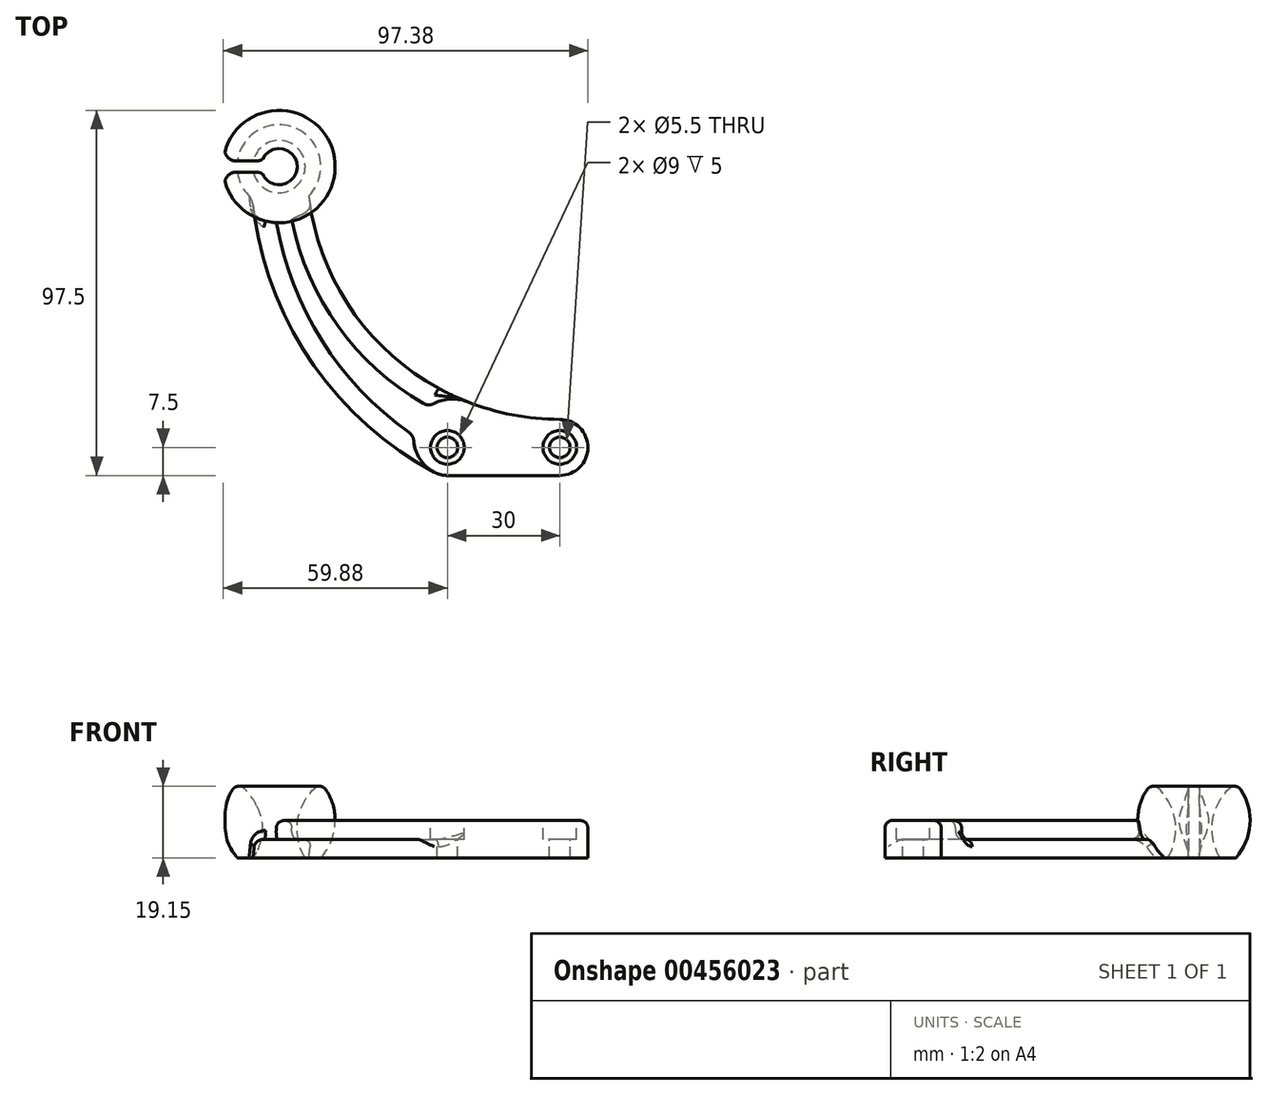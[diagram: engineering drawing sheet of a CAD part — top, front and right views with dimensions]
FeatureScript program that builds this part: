
annotation { "Feature Type Name" : "Feature", "Feature Type Description" : "" }
export const myFeature = defineFeature(function(context is Context, id is Id, definition is map)
    precondition{}
    {
        {
            var Q0;
            Q0=qCreatedBy(makeId("Top.planeOp"),FACE);
            var sketch = newSketch(context, id + "F0", { "sketchPlane" : qUnion([Q0])});
            skLineSegment(sketch, "E0", {"start": v(0, -19.39) * mm, "end": v(0, 110.44) * mm, "construction": true});
            skLineSegment(sketch, "E1.0", {"start": v(10, -19.39) * mm, "end": v(10, 110.44) * mm, "construction": true});
            skLineSegment(sketch, "E2.0", {"start": v(40, -19.39) * mm, "end": v(40, 110.44) * mm, "construction": true});
            skLineSegment(sketch, "E3", {"start": v(61.42, 75) * mm, "end": v(-96.46, 75) * mm, "construction": true});
            skArc(sketch, "E4", {"start": v(-35, 75) * mm, "mid": v(-13.03, 21.97) * mm, "end": v(40, 0) * mm, "construction": true});
            skArc(sketch, "E5.0", {"start": v(-27.5, 75) * mm, "mid": v(-7.73, 27.27) * mm, "end": v(40, 7.5) * mm});
            skArc(sketch, "E6", {"start": v(40, -7.5) * mm, "mid": v(47.5, 0) * mm, "end": v(40, 7.5) * mm});
            skLineSegment(sketch, "E7", {"start": v(40, -7.5) * mm, "end": v(10, -7.5) * mm});
            skArc(sketch, "E8", {"start": v(6.47, -6.62) * mm, "mid": v(8.18, -7.28) * mm, "end": v(10, -7.5) * mm});
            skArc(sketch, "E9", {"start": v(-42.5, 75) * mm, "mid": v(-29.32, 27.4) * mm, "end": v(6.47, -6.62) * mm});
            skPoint(sketch, "E10.orphan", {"position": v(0, -7.5) * mm});
            skLineSegment(sketch, "E11", {"start": v(-42.5, 75) * mm, "end": v(-42.5, 109.62) * mm, "construction": true});
            skLineSegment(sketch, "E12", {"start": v(-42.5, 75) * mm, "end": v(-27.5, 75) * mm});
            skSolve(sketch);
        }
        {
            var Q0;
            Q0 = qSketchRegion(id + "F0", true);
            extrude(context, id + "F1", {"entities" : qUnion([Q0]), "depth" : 5 * mm});
        }
        {
            var Q0;
            Q0=makeQuery(id+"F1.opExtrude","CAP_FACE",FACE,{"disambiguationData":[OSD([sQuery(id+"F0.wireOp",EDGE,"E5.0"),sQuery(id+"F0.wireOp",EDGE,"E6"),sQuery(id+"F0.wireOp",EDGE,"E7"),sQuery(id+"F0.wireOp",EDGE,"E8"),sQuery(id+"F0.wireOp",EDGE,"E9"),sQuery(id+"F0.wireOp",EDGE,"E12")])],"isStart":false});
            var sketch = newSketch(context, id + "F2", { "sketchPlane" : qUnion([Q0])});
            skArc(sketch, "E13.0", {"start": v(6.47, -6.62) * mm, "mid": v(8.18, -7.28) * mm, "end": v(10, -7.5) * mm});
            skLineSegment(sketch, "E14.0", {"start": v(40, -7.5) * mm, "end": v(10, -7.5) * mm});
            skArc(sketch, "E15.0", {"start": v(40, -7.5) * mm, "mid": v(47.5, 0) * mm, "end": v(40, 7.5) * mm});
            skArc(sketch, "E16.0", {"start": v(15.19, 12.23) * mm, "mid": v(27.37, 8.7) * mm, "end": v(40, 7.5) * mm});
            skArc(sketch, "E17", {"start": v(15.19, 12.23) * mm, "mid": v(10.76, 12.94) * mm, "end": v(6.45, 11.72) * mm});
            skArc(sketch, "E18.0", {"start": v(-35, 75) * mm, "mid": v(-13.03, 21.97) * mm, "end": v(40, 0) * mm, "construction": true});
            skArc(sketch, "E19.0", {"start": v(-33, 75) * mm, "mid": v(-23.21, 38.49) * mm, "end": v(3.53, 11.76) * mm});
            skArc(sketch, "E20.0", {"start": v(-37, 75) * mm, "mid": v(-27.27, 35.02) * mm, "end": v(-0.26, 3.99) * mm});
            skArc(sketch, "E21.trimOffspring", {"start": v(1, 1.77) * mm, "mid": v(2.66, -3.13) * mm, "end": v(6.47, -6.62) * mm});
            skPoint(sketch, "E22.orphan", {"position": v(-27.5, 75) * mm});
            skPoint(sketch, "E23.visualSharp", {"position": v(5.12, 10.87) * mm});
            skArc(sketch, "E23.filletArc", {"start": v(3.53, 11.76) * mm, "mid": v(4.98, 11.36) * mm, "end": v(6.45, 11.72) * mm});
            skPoint(sketch, "E24.visualSharp", {"position": v(0.98, 3.12) * mm});
            skArc(sketch, "E24.filletArc", {"start": v(1, 1.77) * mm, "mid": v(0.61, 3.02) * mm, "end": v(-0.26, 3.99) * mm});
            skLineSegment(sketch, "E25", {"start": v(-37, 75) * mm, "end": v(-33, 75) * mm});
            skSolve(sketch);
        }
        {
            var Q0;
            Q0 = qSketchRegion(id + "F2", true);
            extrude(context, id + "F3", {"entities" : qUnion([Q0]), "operationType" : NewBodyOperationType.ADD, "depth" : 5 * mm});
        }
        {
            var Q0;
            Q0=makeQuery(id+"F3.boolean.opBoolean","MERGE",FACE,{"derivedFrom":[makeQuery(id+"F1.opExtrude","SWEPT_FACE",FACE,{"disambiguationData":[OSD([sQuery(id+"F0.wireOp",EDGE,"E12")])]}),makeQuery(id+"F3.opExtrude","SWEPT_FACE",FACE,{"disambiguationData":[OSD([sQuery(id+"F2.wireOp",EDGE,"E25")])]})]});
            var sketch = newSketch(context, id + "F4", { "sketchPlane" : qUnion([Q0])});
            skLineSegment(sketch, "E26", {"start": v(35, -12.3) * mm, "end": v(35, 25.98) * mm, "construction": true});
            skPoint(sketch, "E26.startSnap0", {"position": v(35, 0) * mm});
            skArc(sketch, "E27", {"start": v(22.47, 18.25) * mm, "mid": v(20.04, 8.9) * mm, "end": v(23.82, 0) * mm});
            skLineSegment(sketch, "E28", {"start": v(28, 0) * mm, "end": v(23.82, 0) * mm});
            skArc(sketch, "E29", {"start": v(28, 0) * mm, "mid": v(30.03, 9.73) * mm, "end": v(25.52, 18.6) * mm});
            skPoint(sketch, "E30.visualSharp", {"position": v(23.82, 20) * mm});
            skArc(sketch, "E30.filletArc", {"start": v(25.52, 18.6) * mm, "mid": v(23.92, 19.14) * mm, "end": v(22.47, 18.25) * mm});
            skSolve(sketch);
        }
        {
            var Q0;
            Q0 = qSketchRegion(id + "F4", true);
            var Q1;
            Q1=sQuery(id+"F4.wireOp",EDGE,"E26");
            revolve(context, id + "F5", {"operationType" : NewBodyOperationType.ADD, "entities" : qUnion([Q0]), "axis" : qUnion([Q1]), "revolveType" : RevolveType.FULL});
        }
        {
            var Q0;
            Q0=makeQuery(id+"F3.boolean.opBoolean","MERGE",FACE,{"derivedFrom":[makeQuery(id+"F1.opExtrude","SWEPT_FACE",FACE,{"disambiguationData":[OSD([sQuery(id+"F0.wireOp",EDGE,"E12")])]}),makeQuery(id+"F3.opExtrude","SWEPT_FACE",FACE,{"disambiguationData":[OSD([sQuery(id+"F2.wireOp",EDGE,"E25")])]})]});
            var sketch = newSketch(context, id + "F6", { "sketchPlane" : qUnion([Q0])});
            skArc(sketch, "E31.0", {"start": v(28, 0) * mm, "mid": v(30.03, 9.73) * mm, "end": v(25.52, 18.6) * mm});
            skLineSegment(sketch, "E32.0", {"start": v(35, -12.3) * mm, "end": v(35, 25.98) * mm, "construction": true});
            skLineSegment(sketch, "E33", {"start": v(25.52, 18.6) * mm, "end": v(35, 18.6) * mm});
            skLineSegment(sketch, "E34", {"start": v(35, 18.6) * mm, "end": v(35, 0) * mm});
            skLineSegment(sketch, "E35.0", {"start": v(35, 0) * mm, "end": v(28, 0) * mm});
            skPoint(sketch, "E36.orphan", {"position": v(27.5, 0) * mm});
            skPoint(sketch, "E37.orphan", {"position": v(42.5, 0) * mm});
            skSolve(sketch);
        }
        {
            var Q0;
            Q0 = qSketchRegion(id + "F6", true);
            var Q1;
            Q1=sQuery(id+"F6.wireOp",EDGE,"E32.0");
            revolve(context, id + "F7", {"operationType" : NewBodyOperationType.REMOVE, "entities" : qUnion([Q0]), "axis" : qUnion([Q1]), "revolveType" : RevolveType.FULL, "oppositeDirection" : true});
        }
        {
            var Q0;
            {var subQ0=sQuery(id+"F2.wireOp",EDGE,"E19.0");var subQ1=sQuery(id+"F2.wireOp",EDGE,"E17");var subQ2=sQuery(id+"F2.wireOp",EDGE,"E16.0");var subQ3=sQuery(id+"F2.wireOp",EDGE,"E13.0");var subQ4=sQuery(id+"F2.wireOp",EDGE,"E15.0");var subQ5=sQuery(id+"F2.wireOp",EDGE,"E14.0");var subQ6=sQuery(id+"F2.wireOp",EDGE,"E20.0");var subQ7=sQuery(id+"F2.wireOp",EDGE,"E21.trimOffspring");var subQ8=sQuery(id+"F2.wireOp",EDGE,"E23.filletArc");var subQ9=sQuery(id+"F2.wireOp",EDGE,"E24.filletArc");Q0=makeQuery(id+"F5.boolean.opBoolean","SPLIT",FACE,{"disambiguationData":[TD([makeQuery(id+"F1.opExtrude","SWEPT_FACE",FACE,{"disambiguationData":[OSD([sQuery(id+"F0.wireOp",EDGE,"E5.0")])]})])],"derivedFrom":makeQuery(id+"F3.opExtrude","CAP_FACE",FACE,{"disambiguationData":[OSD([subQ3,subQ5,subQ4,subQ2,subQ1,subQ0,subQ6,subQ7,subQ8,subQ9,sQuery(id+"F2.wireOp",EDGE,"E25")])],"isStart":false})});}
            var sketch = newSketch(context, id + "F8", { "sketchPlane" : qUnion([Q0])});
            skPoint(sketch, "E38.0", {"position": v(10, 0) * mm});
            skPoint(sketch, "E39.0", {"position": v(40, 0) * mm});
            skSolve(sketch);
        }
        {
            var Q0;
            Q0=sQuery(id+"F8.wireOp",VERTEX,"E38.0");
            var Q1;
            Q1=sQuery(id+"F8.wireOp",VERTEX,"E39.0");
            var Q2;
            Q2=makeQuery(id+"F1.opExtrude","SWEPT_BODY",BODY,{"disambiguationData":[OSD([sQuery(id+"F0.wireOp",EDGE,"E5.0"),sQuery(id+"F0.wireOp",EDGE,"E6"),sQuery(id+"F0.wireOp",EDGE,"E7"),sQuery(id+"F0.wireOp",EDGE,"E8"),sQuery(id+"F0.wireOp",EDGE,"E9"),sQuery(id+"F0.wireOp",EDGE,"E12")])]});
            hole(context, id + "F9", {"style" : HoleStyle.C_BORE, "endStyle" : HoleEndStyle.THROUGH, "holeDiameter" : 5.5 * mm, "cBoreDiameter" : 9 * mm, "cBoreDepth" : 5 * mm, "isTappedThrough" : true, "tappedDepth" : 12 * mm, "tapClearance" : 3, "startFromSketch" : true, "locations" : qUnion([Q0, Q1]), "scope" : qUnion([Q2])});
        }
        {
            var Q0;
            {var subQ0=sQuery(id+"F2.wireOp",EDGE,"E24.filletArc");var subQ1=sQuery(id+"F2.wireOp",EDGE,"E20.0");Q0=makeQuery(id+"F5.boolean.opBoolean","SPLIT",EDGE,{"disambiguationData":[TD([makeQuery(id+"F3.opExtrude","SWEPT_FACE",FACE,{"disambiguationData":[OSD([subQ0])]})])],"derivedFrom":makeQuery(id+"F3.opExtrude","CAP_EDGE",EDGE,{"disambiguationData":[OSD([subQ1])],"isStart":false})});}
            var Q1;
            Q1=makeQuery(id+"F1.opExtrude","CAP_EDGE",EDGE,{"disambiguationData":[OSD([sQuery(id+"F0.wireOp",EDGE,"E9")])],"isStart":false});
            fillet(context, id + "F10", {"entities" : qUnion([Q0, Q1]), "radius" : 2 * mm, "tangentPropagation" : true, "allowEdgeOverflow" : false});
        }
        {
            var Q0;
            {var subQ0=sQuery(id+"F2.wireOp",EDGE,"E20.0");Q0=makeQuery(id+"F5.boolean.opBoolean","SPLIT",EDGE,{"disambiguationData":[TD([makeQuery(id+"F3.opExtrude","SWEPT_FACE",FACE,{"disambiguationData":[OSD([sQuery(id+"F2.wireOp",EDGE,"E24.filletArc")])]})])],"derivedFrom":makeQuery(id+"F3.opExtrude","CAP_EDGE",EDGE,{"disambiguationData":[OSD([subQ0])],"isStart":true})});}
            var Q1;
            Q1=makeQuery(id+"F1.opExtrude","CAP_EDGE",EDGE,{"disambiguationData":[OSD([sQuery(id+"F0.wireOp",EDGE,"E5.0")])],"isStart":false});
            var Q2;
            {var subQ0=sQuery(id+"F2.wireOp",EDGE,"E19.0");Q2=makeQuery(id+"F5.boolean.opBoolean","SPLIT",EDGE,{"disambiguationData":[TD([makeQuery(id+"F3.opExtrude","SWEPT_FACE",FACE,{"disambiguationData":[OSD([sQuery(id+"F2.wireOp",EDGE,"E23.filletArc")])]})])],"derivedFrom":makeQuery(id+"F3.opExtrude","CAP_EDGE",EDGE,{"disambiguationData":[OSD([subQ0])],"isStart":true})});}
            fillet(context, id + "F11", {"entities" : qUnion([Q0, Q1, Q2]), "radius" : 2 * mm, "tangentPropagation" : true, "allowEdgeOverflow" : false});
        }
        {
            var Q0;
            {var subQ0=sQuery(id+"F0.wireOp",EDGE,"E12");var subQ1=sQuery(id+"F0.wireOp",EDGE,"E9");var subQ2=sQuery(id+"F0.wireOp",EDGE,"E8");Q0=makeQuery(id+"F5.boolean.opBoolean","INTERSECT",EDGE,{"derivedFrom":[makeQuery(id+"F3.boolean.opBoolean","SPLIT",FACE,{"disambiguationData":[TD([makeQuery(id+"F1.opExtrude","SWEPT_FACE",FACE,{"disambiguationData":[OSD([subQ2])]})])],"derivedFrom":makeQuery(id+"F1.opExtrude","CAP_FACE",FACE,{"disambiguationData":[OSD([sQuery(id+"F0.wireOp",EDGE,"E5.0"),sQuery(id+"F0.wireOp",EDGE,"E6"),sQuery(id+"F0.wireOp",EDGE,"E7"),subQ2,subQ1,subQ0])],"isStart":false})}),makeQuery(id+"F5.opRevolve","SWEPT_FACE",FACE,{"disambiguationData":[OSD([sQuery(id+"F4.wireOp",EDGE,"E27")])]})]});}
            fillet(context, id + "F12", {"entities" : qUnion([Q0]), "radius" : 2 * mm, "tangentPropagation" : true, "allowEdgeOverflow" : false});
        }
        {
            var Q0;
            Q0=qCreatedBy(makeId("Top.planeOp"),FACE);
            var sketch = newSketch(context, id + "F13", { "sketchPlane" : qUnion([Q0])});
            skLineSegment(sketch, "E40.0", {"start": v(-20, 75) * mm, "end": v(-96.46, 75) * mm, "construction": true});
            skArc(sketch, "E41", {"start": v(-39.44, 76.94) * mm, "mid": v(-39.74, 76) * mm, "end": v(-39.84, 75) * mm});
            skArc(sketch, "E42", {"start": v(-30.31, 60.75) * mm, "mid": v(-22.85, 66.2) * mm, "end": v(-20, 75) * mm});
            skArc(sketch, "E43", {"start": v(-41, 76.5) * mm, "mid": v(-40.19, 76.61) * mm, "end": v(-39.44, 76.94) * mm});
            skArc(sketch, "E44", {"start": v(-49.46, 79) * mm, "mid": v(-48.44, 77.2) * mm, "end": v(-46.5, 76.5) * mm});
            skArc(sketch, "E45.trimOffspring", {"start": v(-49.46, 79) * mm, "mid": v(-49.86, 77.02) * mm, "end": v(-50, 75) * mm});
            skLineSegment(sketch, "E46.trimOffspring", {"start": v(-41, 76.5) * mm, "end": v(-46.5, 76.5) * mm});
            skArc(sketch, "E47.MirrorCS", {"start": v(-41, 73.5) * mm, "mid": v(-40.19, 73.39) * mm, "end": v(-39.44, 73.06) * mm});
            skArc(sketch, "E48.MirrorCS", {"start": v(-39.44, 73.06) * mm, "mid": v(-39.74, 74) * mm, "end": v(-39.84, 75) * mm});
            skLineSegment(sketch, "E49.MirrorCS", {"start": v(-41, 73.5) * mm, "end": v(-46.5, 73.5) * mm});
            skArc(sketch, "E50.MirrorCS", {"start": v(-49.46, 71) * mm, "mid": v(-48.44, 72.8) * mm, "end": v(-46.5, 73.5) * mm});
            skArc(sketch, "E51.MirrorCS", {"start": v(-49.46, 71) * mm, "mid": v(-49.86, 72.98) * mm, "end": v(-50, 75) * mm});
            skPoint(sketch, "E52.orphan", {"position": v(61.42, 75) * mm});
            skSolve(sketch);
        }
        {
            var Q0;
            Q0 = qSketchRegion(id + "F13", true);
            extrude(context, id + "F14", {"entities" : qUnion([Q0]), "operationType" : NewBodyOperationType.REMOVE, "depth" : 25 * mm});
        }
    });
